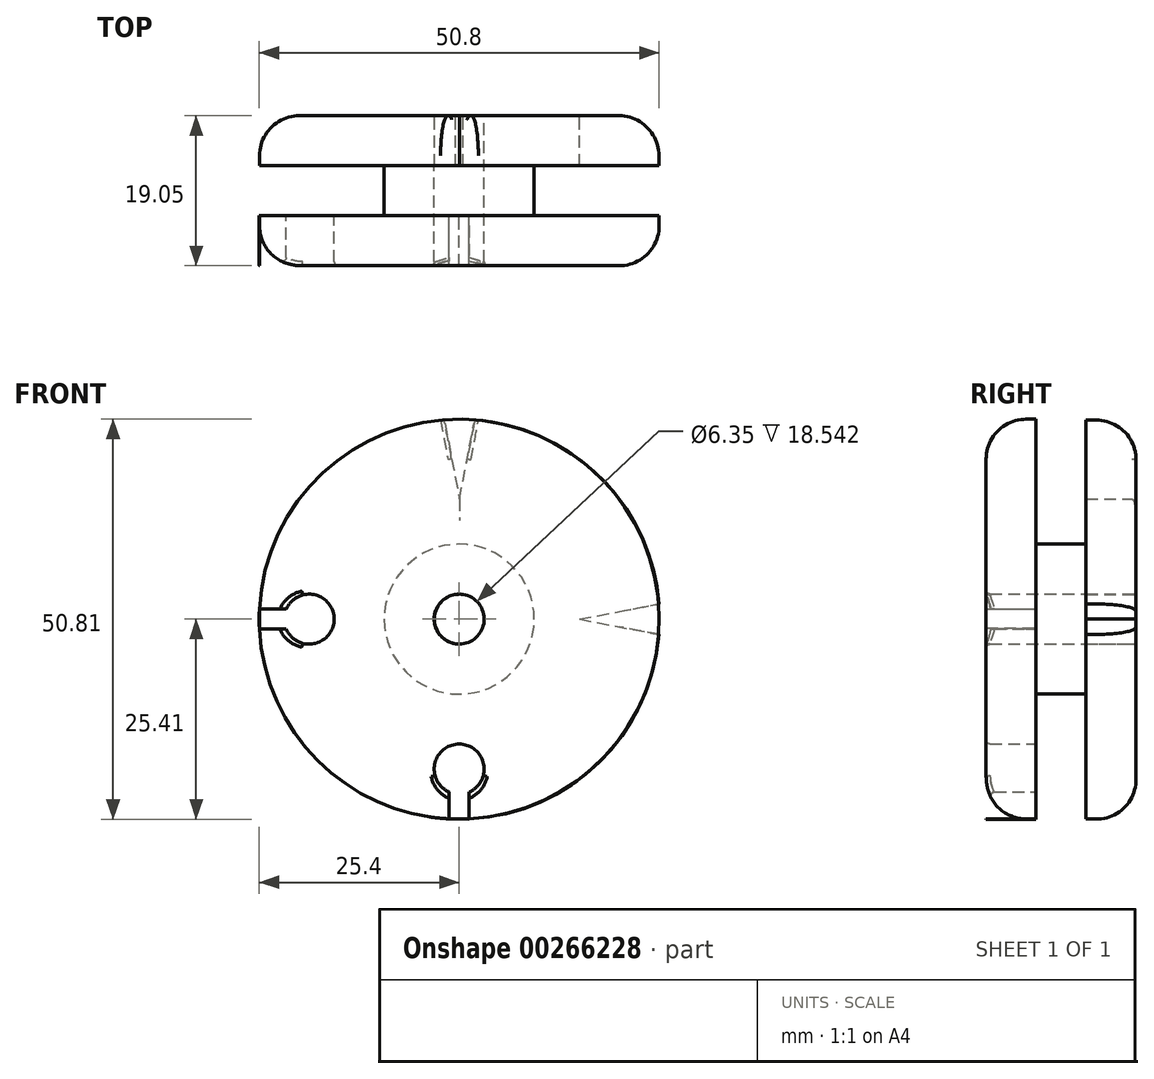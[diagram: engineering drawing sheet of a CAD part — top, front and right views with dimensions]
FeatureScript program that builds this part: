
annotation { "Feature Type Name" : "Feature", "Feature Type Description" : "" }
export const myFeature = defineFeature(function(context is Context, id is Id, definition is map)
    precondition{}
    {
        {
            var Q0;
            Q0=qCreatedBy(makeId("Front.planeOp"),FACE);
            var sketch = newSketch(context, id + "F0", { "sketchPlane" : qUnion([Q0])});
            skCircle(sketch, "E0", {"center": v(0.04, 0) * mm, "radius": 25.4 * mm});
            skCircle(sketch, "E1", {"center": v(0.04, 0) * mm, "radius": 3.18 * mm});
            skLineSegment(sketch, "E2", {"start": v(0.04, 0) * mm, "end": v(31.79, 0) * mm});
            skLineSegment(sketch, "E3", {"start": v(0.04, 0) * mm, "end": v(0.04, 31.74) * mm});
            skLineSegment(sketch, "E4", {"start": v(31.79, 0) * mm, "end": v(31.79, 3.17) * mm});
            skLineSegment(sketch, "E5", {"start": v(31.79, 0) * mm, "end": v(31.79, -3.18) * mm});
            skLineSegment(sketch, "E6", {"start": v(0.04, 31.74) * mm, "end": v(-3.14, 31.74) * mm});
            skLineSegment(sketch, "E7", {"start": v(0.04, 31.74) * mm, "end": v(3.21, 31.74) * mm});
            skLineSegment(sketch, "E8", {"start": v(31.79, 0) * mm, "end": v(15.28, 0) * mm});
            skLineSegment(sketch, "E9", {"start": v(15.28, 0) * mm, "end": v(31.79, 3.17) * mm});
            skLineSegment(sketch, "E10", {"start": v(15.28, 0) * mm, "end": v(31.79, -3.18) * mm});
            skLineSegment(sketch, "E11", {"start": v(0.04, 31.74) * mm, "end": v(0.04, 15.23) * mm});
            skLineSegment(sketch, "E12", {"start": v(-3.14, 31.74) * mm, "end": v(0.04, 15.23) * mm});
            skLineSegment(sketch, "E13", {"start": v(0.04, 15.23) * mm, "end": v(3.21, 31.74) * mm});
            skSolve(sketch);
        }
        {
            var Q0;
            {var subQ5=sQuery(id+"F0.wireOp",EDGE,"E12");var subQ7=sQuery(id+"F0.wireOp",EDGE,"E0");var subQ8=makeQuery(id+"F0.imprint","INTERSECT",VERTEX,{"derivedFrom":[subQ7,subQ5]});Q0=makeQuery(id+"F0.imprint","IMPRINT",FACE,{"disambiguationData":[TD([[makeQuery(id+"F0.imprint","IMPRINT",EDGE,{"disambiguationData":[TD([[subQ8,-1.0]])],"derivedFrom":subQ7}),1.0]])]});}
            var Q1;
            {var subQ5=sQuery(id+"F0.wireOp",EDGE,"E9");var subQ9=sQuery(id+"F0.wireOp",EDGE,"E0");var subQ10=makeQuery(id+"F0.imprint","INTERSECT",VERTEX,{"derivedFrom":[subQ9,subQ5]});Q1=makeQuery(id+"F0.imprint","IMPRINT",FACE,{"disambiguationData":[TD([[makeQuery(id+"F0.imprint","IMPRINT",EDGE,{"disambiguationData":[TD([[subQ10,-1.0]])],"derivedFrom":subQ9}),1.0]])]});}
            extrude(context, id + "F1", {"entities" : qUnion([Q0, Q1]), "depth" : 6.35 * mm});
        }
        {
            var Q0;
            Q0=qCreatedBy(makeId("Front.planeOp"),FACE);
            var sketch = newSketch(context, id + "F2", { "sketchPlane" : qUnion([Q0])});
            skCircle(sketch, "E14", {"center": v(0, 0) * mm, "radius": 9.53 * mm});
            skCircle(sketch, "E15", {"center": v(0, 0) * mm, "radius": 3.18 * mm});
            skSolve(sketch);
        }
        {
            var Q0;
            Q0 = qSketchRegion(id + "F2", true);
            extrude(context, id + "F3", {"entities" : qUnion([Q0]), "operationType" : NewBodyOperationType.ADD, "depth" : 12.7 * mm});
        }
        {
            var Q0;
            Q0=makeQuery(id+"F3.opExtrude","CAP_FACE",FACE,{"disambiguationData":[OSD([sQuery(id+"F2.wireOp",EDGE,"E14"),sQuery(id+"F2.wireOp",EDGE,"E15")])],"isStart":false});
            var sketch = newSketch(context, id + "F4", { "sketchPlane" : qUnion([Q0])});
            skCircle(sketch, "E16", {"center": v(0, 0) * mm, "radius": 3.18 * mm});
            skCircle(sketch, "E17", {"center": v(0, 0) * mm, "radius": 25.4 * mm});
            skLineSegment(sketch, "E18", {"start": v(-25.4, 0) * mm, "end": v(-19.05, 0) * mm});
            skLineSegment(sketch, "E19", {"start": v(0, -25.4) * mm, "end": v(0, -19.05) * mm});
            skLineSegment(sketch, "E20", {"start": v(0, -19.05) * mm, "end": v(1.27, -19.05) * mm});
            skLineSegment(sketch, "E21", {"start": v(0, -25.4) * mm, "end": v(-1.27, -25.4) * mm});
            skLineSegment(sketch, "E22", {"start": v(0, -19.05) * mm, "end": v(-1.27, -19.05) * mm});
            skLineSegment(sketch, "E23", {"start": v(0, -25.4) * mm, "end": v(1.25, -25.4) * mm});
            skCircle(sketch, "E24", {"center": v(0, -19.05) * mm, "radius": 3.18 * mm});
            skCircle(sketch, "E25", {"center": v(-19.05, 0) * mm, "radius": 3.18 * mm});
            skLineSegment(sketch, "E26.bottom", {"start": v(-19.05, 0) * mm, "end": v(-25.37, 0) * mm});
            skLineSegment(sketch, "E26.left", {"start": v(-19.05, 0) * mm, "end": v(-19.04, 1.27) * mm});
            skLineSegment(sketch, "E26.right", {"start": v(-25.37, 0) * mm, "end": v(-25.37, 1.27) * mm});
            skLineSegment(sketch, "E27.bottom", {"start": v(-25.37, 0) * mm, "end": v(-19.05, 0) * mm});
            skLineSegment(sketch, "E27.left", {"start": v(-25.37, 0) * mm, "end": v(-25.37, -1.27) * mm});
            skLineSegment(sketch, "E27.right", {"start": v(-19.05, 0) * mm, "end": v(-19.05, -1.27) * mm});
            skLineSegment(sketch, "E28", {"start": v(-19.04, 1.27) * mm, "end": v(-25.37, 1.27) * mm});
            skLineSegment(sketch, "E29", {"start": v(-25.37, 1.27) * mm, "end": v(-28.63, 1.27) * mm});
            skLineSegment(sketch, "E30", {"start": v(-28.63, 1.27) * mm, "end": v(-26.5, -1.3) * mm});
            skLineSegment(sketch, "E31", {"start": v(-26.5, -1.3) * mm, "end": v(-25.37, -1.27) * mm});
            skLineSegment(sketch, "E32", {"start": v(-25.37, -1.27) * mm, "end": v(-19.05, -1.27) * mm});
            skLineSegment(sketch, "E33.bottom", {"start": v(-1.27, -19.05) * mm, "end": v(1.25, -19.05) * mm});
            skLineSegment(sketch, "E33.top", {"start": v(-1.27, -25.96) * mm, "end": v(1.25, -25.96) * mm});
            skLineSegment(sketch, "E33.left", {"start": v(-1.27, -19.05) * mm, "end": v(-1.27, -25.96) * mm});
            skLineSegment(sketch, "E33.right", {"start": v(1.25, -19.05) * mm, "end": v(1.25, -25.96) * mm});
            skSolve(sketch);
        }
        {
            var Q0;
            {var subQ0=sQuery(id+"F4.wireOp",EDGE,"E21");Q0=makeQuery(id+"F4.imprint","IMPRINT",FACE,{"disambiguationData":[TD([[makeQuery(id+"F4.imprint","IMPRINT",EDGE,{"derivedFrom":subQ0}),-1.0]])]});}
            var Q1;
            {var subQ0=sQuery(id+"F4.wireOp",EDGE,"E23");Q1=makeQuery(id+"F4.imprint","IMPRINT",FACE,{"disambiguationData":[TD([[makeQuery(id+"F4.imprint","IMPRINT",EDGE,{"derivedFrom":subQ0}),1.0]])]});}
            var Q2;
            Q2=makeQuery(id+"F4.imprint","IMPRINT",FACE,{"disambiguationData":[TD([[makeQuery(id+"F4.imprint","IMPRINT",EDGE,{"derivedFrom":sQuery(id+"F4.wireOp",EDGE,"E16")}),-1.0]])]});
            var Q3;
            {var subQ0=sQuery(id+"F4.wireOp",EDGE,"E18");Q3=makeQuery(id+"F4.imprint","IMPRINT",FACE,{"disambiguationData":[TD([[makeQuery(id+"F4.imprint","IMPRINT",EDGE,{"derivedFrom":subQ0}),1.0]])]});}
            var Q4;
            {var subQ0=sQuery(id+"F4.wireOp",EDGE,"E18");Q4=makeQuery(id+"F4.imprint","IMPRINT",FACE,{"disambiguationData":[TD([[makeQuery(id+"F4.imprint","IMPRINT",EDGE,{"derivedFrom":subQ0}),-1.0]])]});}
            var Q5;
            Q5=makeQuery(id+"F4.imprint","IMPRINT",FACE,{"disambiguationData":[TD([[makeQuery(id+"F4.imprint","IMPRINT",EDGE,{"derivedFrom":makeQuery(id+"F3.opExtrude","CAP_EDGE",EDGE,{"disambiguationData":[OSD([sQuery(id+"F2.wireOp",EDGE,"E14")])],"isStart":false})}),-1.0]])]});
            extrude(context, id + "F5", {"entities" : qUnion([Q0, Q1, Q2, Q3, Q4, Q5]), "operationType" : NewBodyOperationType.ADD, "depth" : 6.35 * mm});
        }
        {
            var Q0;
            {var subQ0=sQuery(id+"F4.wireOp",EDGE,"E17");Q0=makeQuery(id+"F5.opExtrude","CAP_EDGE",EDGE,{"disambiguationData":[OSD([subQ0]),TDD([makeQuery(id+"F4.imprint","IMPRINT",EDGE,{"disambiguationData":[TD([[makeQuery(id+"F4.imprint","INTERSECT",VERTEX,{"derivedFrom":[subQ0,sQuery(id+"F4.wireOp",EDGE,"E33.right")]}),-1.0]])],"derivedFrom":subQ0})])],"isStart":false});}
            var Q1;
            {var subQ0=sQuery(id+"F0.wireOp",EDGE,"E0");Q1=makeQuery(id+"F1.opExtrude","CAP_EDGE",EDGE,{"disambiguationData":[OSD([subQ0]),TDD([makeQuery(id+"F0.imprint","IMPRINT",EDGE,{"disambiguationData":[TD([[makeQuery(id+"F0.imprint","INTERSECT",VERTEX,{"derivedFrom":[subQ0,sQuery(id+"F0.wireOp",EDGE,"E9")]}),-1.0]])],"derivedFrom":subQ0})])],"isStart":true});}
            var Q2;
            {var subQ0=sQuery(id+"F0.wireOp",EDGE,"E0");Q2=makeQuery(id+"F1.opExtrude","CAP_EDGE",EDGE,{"disambiguationData":[OSD([subQ0]),TDD([makeQuery(id+"F0.imprint","IMPRINT",EDGE,{"disambiguationData":[TD([[makeQuery(id+"F0.imprint","INTERSECT",VERTEX,{"derivedFrom":[subQ0,sQuery(id+"F0.wireOp",EDGE,"E12")]}),-1.0]])],"derivedFrom":subQ0})])],"isStart":true});}
            var Q3;
            {var subQ0=sQuery(id+"F4.wireOp",EDGE,"E17");Q3=makeQuery(id+"F5.opExtrude","CAP_EDGE",EDGE,{"disambiguationData":[OSD([subQ0]),TDD([makeQuery(id+"F4.imprint","IMPRINT",EDGE,{"disambiguationData":[TD([[makeQuery(id+"F4.imprint","INTERSECT",VERTEX,{"derivedFrom":[subQ0,sQuery(id+"F4.wireOp",EDGE,"E32")]}),-1.0]])],"derivedFrom":subQ0})])],"isStart":false});}
            fillet(context, id + "F6", {"entities" : qUnion([Q0, Q1, Q2, Q3]), "radius" : 5.08 * mm, "tangentPropagation" : true, "allowEdgeOverflow" : false});
        }
        {
            var Q0;
            Q0=makeQuery(id+"F5.opExtrude","CAP_EDGE",EDGE,{"disambiguationData":[OSD([sQuery(id+"F4.wireOp",EDGE,"E25")])],"isStart":false});
            var Q1;
            {var subQ0=sQuery(id+"F4.wireOp",EDGE,"E17");Q1=makeQuery(id+"F6.opFillet","BLEND_EDGE",EDGE,{"blendedFrom":[makeQuery(id+"F5.opExtrude","CAP_EDGE",EDGE,{"disambiguationData":[OSD([subQ0]),TDD([makeQuery(id+"F4.imprint","IMPRINT",EDGE,{"disambiguationData":[TD([[makeQuery(id+"F4.imprint","INTERSECT",VERTEX,{"derivedFrom":[subQ0,sQuery(id+"F4.wireOp",EDGE,"E32")]}),-1.0]])],"derivedFrom":subQ0})])],"isStart":false}),makeQuery(id+"F5.opExtrude","SWEPT_FACE",FACE,{"disambiguationData":[OSD([sQuery(id+"F4.wireOp",EDGE,"E25")])]})],"blendedInto":[makeQuery(id+"F5.opExtrude","SWEPT_FACE",FACE,{"disambiguationData":[OSD([sQuery(id+"F4.wireOp",EDGE,"E25")])]})]});}
            var Q2;
            {var subQ0=sQuery(id+"F4.wireOp",EDGE,"E17");Q2=makeQuery(id+"F6.opFillet","BLEND_EDGE",EDGE,{"blendedFrom":[makeQuery(id+"F5.opExtrude","CAP_EDGE",EDGE,{"disambiguationData":[OSD([subQ0]),TDD([makeQuery(id+"F4.imprint","IMPRINT",EDGE,{"disambiguationData":[TD([[makeQuery(id+"F4.imprint","INTERSECT",VERTEX,{"derivedFrom":[subQ0,sQuery(id+"F4.wireOp",EDGE,"E33.right")]}),-1.0]])],"derivedFrom":subQ0})])],"isStart":false}),makeQuery(id+"F5.opExtrude","SWEPT_FACE",FACE,{"disambiguationData":[OSD([sQuery(id+"F4.wireOp",EDGE,"E25")])]})],"blendedInto":[makeQuery(id+"F5.opExtrude","SWEPT_FACE",FACE,{"disambiguationData":[OSD([sQuery(id+"F4.wireOp",EDGE,"E25")])]})]});}
            var Q3;
            Q3=makeQuery(id+"F5.opExtrude","CAP_EDGE",EDGE,{"disambiguationData":[OSD([sQuery(id+"F4.wireOp",EDGE,"E24")])],"isStart":false});
            var Q4;
            {var subQ0=sQuery(id+"F4.wireOp",EDGE,"E17");Q4=makeQuery(id+"F6.opFillet","BLEND_EDGE",EDGE,{"blendedFrom":[makeQuery(id+"F5.opExtrude","CAP_EDGE",EDGE,{"disambiguationData":[OSD([subQ0]),TDD([makeQuery(id+"F4.imprint","IMPRINT",EDGE,{"disambiguationData":[TD([[makeQuery(id+"F4.imprint","INTERSECT",VERTEX,{"derivedFrom":[subQ0,sQuery(id+"F4.wireOp",EDGE,"E32")]}),-1.0]])],"derivedFrom":subQ0})])],"isStart":false}),makeQuery(id+"F5.opExtrude","SWEPT_FACE",FACE,{"disambiguationData":[OSD([sQuery(id+"F4.wireOp",EDGE,"E24")])]})],"blendedInto":[makeQuery(id+"F5.opExtrude","SWEPT_FACE",FACE,{"disambiguationData":[OSD([sQuery(id+"F4.wireOp",EDGE,"E24")])]})]});}
            var Q5;
            {var subQ0=sQuery(id+"F4.wireOp",EDGE,"E17");Q5=makeQuery(id+"F6.opFillet","BLEND_EDGE",EDGE,{"blendedFrom":[makeQuery(id+"F5.opExtrude","CAP_EDGE",EDGE,{"disambiguationData":[OSD([subQ0]),TDD([makeQuery(id+"F4.imprint","IMPRINT",EDGE,{"disambiguationData":[TD([[makeQuery(id+"F4.imprint","INTERSECT",VERTEX,{"derivedFrom":[subQ0,sQuery(id+"F4.wireOp",EDGE,"E33.right")]}),-1.0]])],"derivedFrom":subQ0})])],"isStart":false}),makeQuery(id+"F5.opExtrude","SWEPT_FACE",FACE,{"disambiguationData":[OSD([sQuery(id+"F4.wireOp",EDGE,"E24")])]})],"blendedInto":[makeQuery(id+"F5.opExtrude","SWEPT_FACE",FACE,{"disambiguationData":[OSD([sQuery(id+"F4.wireOp",EDGE,"E24")])]})]});}
            var Q6;
            Q6=makeQuery(id+"F5.opExtrude","CAP_EDGE",EDGE,{"disambiguationData":[OSD([sQuery(id+"F4.wireOp",EDGE,"E16")])],"isStart":false});
            var Q7;
            Q7=makeQuery(id+"F1.opExtrude","CAP_EDGE",EDGE,{"disambiguationData":[OSD([sQuery(id+"F0.wireOp",EDGE,"E13")])],"isStart":true});
            var Q8;
            Q8=makeQuery(id+"F1.opExtrude","CAP_EDGE",EDGE,{"disambiguationData":[OSD([sQuery(id+"F0.wireOp",EDGE,"E12")])],"isStart":true});
            fillet(context, id + "F7", {"entities" : qUnion([Q0, Q1, Q2, Q3, Q4, Q5, Q6, Q7, Q8]), "radius" : 0.5 * mm, "tangentPropagation" : true, "allowEdgeOverflow" : false});
        }
    });
